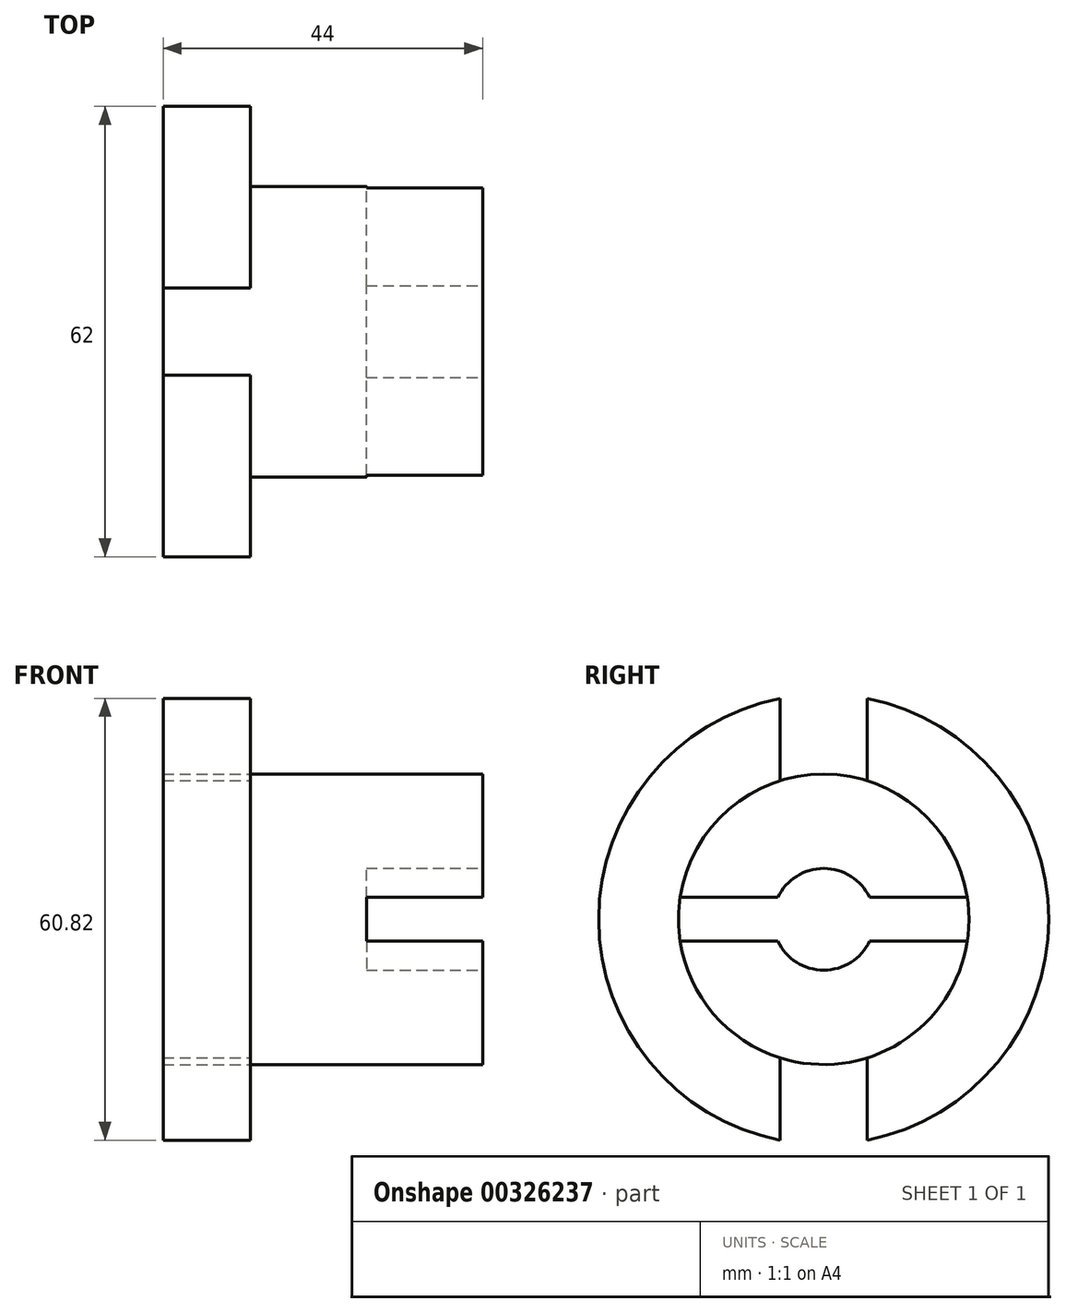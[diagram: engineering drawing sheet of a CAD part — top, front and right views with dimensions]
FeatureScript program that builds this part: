
annotation { "Feature Type Name" : "Feature", "Feature Type Description" : "" }
export const myFeature = defineFeature(function(context is Context, id is Id, definition is map)
    precondition{}
    {
        {
            var Q0;
            Q0=qCreatedBy(makeId("Right.planeOp"),FACE);
            var sketch = newSketch(context, id + "F0", { "sketchPlane" : qUnion([Q0])});
            skCircle(sketch, "E0", {"center": v(0, 0) * mm, "radius": 31 * mm});
            skSolve(sketch);
        }
        {
            var Q0;
            Q0 = qSketchRegion(id + "F0", true);
            extrude(context, id + "F1", {"entities" : qUnion([Q0]), "depth" : 44 * mm});
        }
        {
            var Q0;
            Q0=makeQuery(id+"F1.opExtrude","CAP_FACE",FACE,{"disambiguationData":[OSD([sQuery(id+"F0.wireOp",EDGE,"E0")])],"isStart":false});
            var sketch = newSketch(context, id + "F2", { "sketchPlane" : qUnion([Q0])});
            skCircle(sketch, "E1", {"center": v(0, 0) * mm, "radius": 20 * mm});
            skSolve(sketch);
        }
        {
            var Q0;
            Q0=makeQuery(id+"F2.imprint","IMPRINT",FACE,{"disambiguationData":[TD([[makeQuery(id+"F2.imprint","IMPRINT",EDGE,{"derivedFrom":sQuery(id+"F2.wireOp",EDGE,"E1")}),-1.0]])]});
            extrude(context, id + "F3", {"entities" : qUnion([Q0]), "operationType" : NewBodyOperationType.REMOVE, "oppositeDirection" : true, "depth" : 32 * mm});
        }
        {
            var Q0;
            Q0=makeQuery(id+"F3.boolean.opBoolean","COPY",FACE,{"derivedFrom":makeQuery(id+"F3.opExtrude","CAP_FACE",FACE,{"disambiguationData":[OSD([sQuery(id+"F0.wireOp",EDGE,"E0"),sQuery(id+"F2.wireOp",EDGE,"E1")])],"isStart":false})});
            var sketch = newSketch(context, id + "F4", { "sketchPlane" : qUnion([Q0])});
            skLineSegment(sketch, "E2", {"start": v(0, 39.93) * mm, "end": v(0, -44.91) * mm, "construction": true});
            skLineSegment(sketch, "E3", {"start": v(-6, 30.41) * mm, "end": v(-6, 19.08) * mm});
            skLineSegment(sketch, "E4", {"start": v(6, 30.41) * mm, "end": v(6, 19.08) * mm});
            skLineSegment(sketch, "E5", {"start": v(6, -19.08) * mm, "end": v(6, -30.41) * mm});
            skLineSegment(sketch, "E6", {"start": v(-6, -19.08) * mm, "end": v(-6, -30.41) * mm});
            skSolve(sketch);
        }
        {
            var Q0;
            {var subQ0=sQuery(id+"F4.wireOp",EDGE,"E3");Q0=makeQuery(id+"F4.imprint","IMPRINT",FACE,{"disambiguationData":[TD([[makeQuery(id+"F4.imprint","IMPRINT",EDGE,{"derivedFrom":subQ0}),1.0]])]});}
            var Q1;
            {var subQ0=sQuery(id+"F4.wireOp",EDGE,"E5");Q1=makeQuery(id+"F4.imprint","IMPRINT",FACE,{"disambiguationData":[TD([[makeQuery(id+"F4.imprint","IMPRINT",EDGE,{"derivedFrom":subQ0}),-1.0]])]});}
            extrude(context, id + "F5", {"entities" : qUnion([Q0, Q1]), "operationType" : NewBodyOperationType.REMOVE, "oppositeDirection" : true, "depth" : 25 * mm});
        }
        {
            var Q0;
            Q0=makeQuery(id+"F1.opExtrude","CAP_FACE",FACE,{"disambiguationData":[OSD([sQuery(id+"F0.wireOp",EDGE,"E0")])],"isStart":false});
            var sketch = newSketch(context, id + "F6", { "sketchPlane" : qUnion([Q0])});
            skArc(sketch, "E7", {"start": v(-6.32, -3) * mm, "mid": v(0, -7) * mm, "end": v(6.32, -3) * mm});
            skLineSegment(sketch, "E8", {"start": v(-19.77, 3) * mm, "end": v(-6.32, 3) * mm});
            skLineSegment(sketch, "E9", {"start": v(-19.77, -3) * mm, "end": v(-6.32, -3) * mm});
            skLineSegment(sketch, "E10", {"start": v(-29.98, 0) * mm, "end": v(26.21, 0) * mm, "construction": true});
            skLineSegment(sketch, "E11.trimOffspring", {"start": v(6.32, 3) * mm, "end": v(19.77, 3) * mm});
            skLineSegment(sketch, "E12.trimOffspring", {"start": v(6.32, -3) * mm, "end": v(19.77, -3) * mm});
            skArc(sketch, "E13.trimOffspring", {"start": v(6.32, 3) * mm, "mid": v(0, 7) * mm, "end": v(-6.32, 3) * mm});
            skSolve(sketch);
        }
        {
            var Q0;
            Q0=makeQuery(id+"F6.imprint","IMPRINT",FACE,{"disambiguationData":[TD([[makeQuery(id+"F6.imprint","IMPRINT",EDGE,{"derivedFrom":sQuery(id+"F6.wireOp",EDGE,"E7")}),1.0]])]});
            extrude(context, id + "F7", {"entities" : qUnion([Q0]), "operationType" : NewBodyOperationType.REMOVE, "oppositeDirection" : true, "depth" : 16 * mm});
        }
    });
